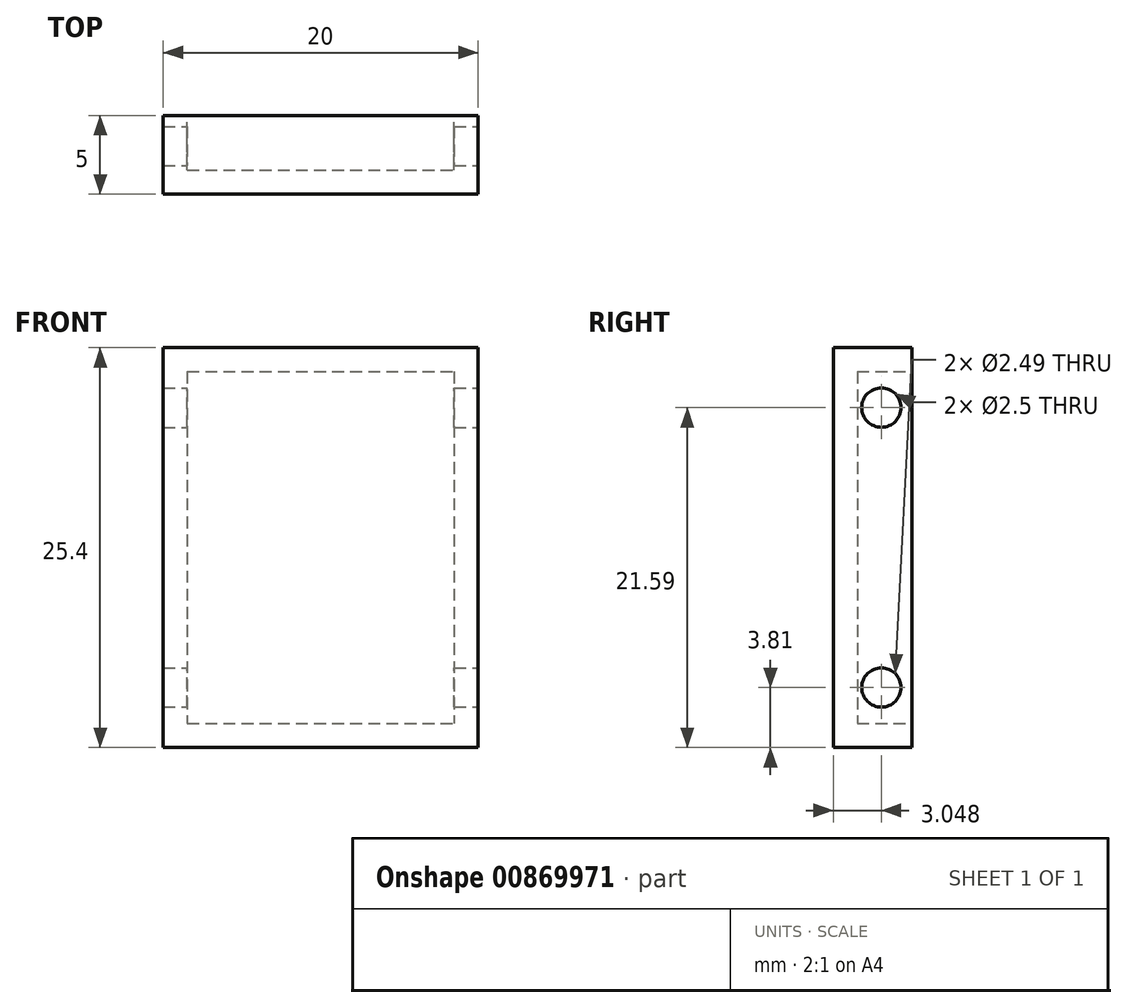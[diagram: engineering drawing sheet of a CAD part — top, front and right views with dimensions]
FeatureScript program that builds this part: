
annotation { "Feature Type Name" : "Feature", "Feature Type Description" : "" }
export const myFeature = defineFeature(function(context is Context, id is Id, definition is map)
    precondition{}
    {
        {
            var Q0;
            Q0=qCreatedBy(makeId("Front.planeOp"),FACE);
            var sketch = newSketch(context, id + "F0", { "sketchPlane" : qUnion([Q0])});
            skLineSegment(sketch, "E0.bottom", {"start": v(-10, 12.7) * mm, "end": v(10, 12.7) * mm});
            skLineSegment(sketch, "E0.top", {"start": v(-10, -12.7) * mm, "end": v(10, -12.7) * mm});
            skLineSegment(sketch, "E0.left", {"start": v(-10, 12.7) * mm, "end": v(-10, -12.7) * mm});
            skLineSegment(sketch, "E0.right", {"start": v(10, 12.7) * mm, "end": v(10, -12.7) * mm});
            skSolve(sketch);
        }
        {
            var Q0;
            Q0 = qSketchRegion(id + "F0", true);
            extrude(context, id + "F1", {"entities" : qUnion([Q0]), "depth" : 5 * mm, "offsetDistance" : 25.4 * mm});
        }
        {
            var Q0;
            Q0=makeQuery(id+"F1.opExtrude","CAP_FACE",FACE,{"disambiguationData":[OSD([sQuery(id+"F0.wireOp",EDGE,"E0.bottom"),sQuery(id+"F0.wireOp",EDGE,"E0.top"),sQuery(id+"F0.wireOp",EDGE,"E0.left"),sQuery(id+"F0.wireOp",EDGE,"E0.right")])],"isStart":true});
            shell(context, id + "F2", {"entities" : qUnion([Q0]), "thickness" : 1.52 * mm});
        }
        {
            var Q0;
            Q0=makeQuery(id+"F1.opExtrude","SWEPT_FACE",FACE,{"disambiguationData":[OSD([sQuery(id+"F0.wireOp",EDGE,"E0.right")])]});
            var sketch = newSketch(context, id + "F3", { "sketchPlane" : qUnion([Q0])});
            skCircle(sketch, "E1", {"center": v(-1.95, 8.89) * mm, "radius": 1.25 * mm});
            skCircle(sketch, "E2", {"center": v(-1.95, -8.9) * mm, "radius": 1.24 * mm});
            skSolve(sketch);
        }
        {
            var Q0;
            Q0=makeQuery(id+"F3.imprint","IMPRINT",FACE,{"disambiguationData":[TD([[makeQuery(id+"F3.imprint","IMPRINT",EDGE,{"derivedFrom":sQuery(id+"F3.wireOp",EDGE,"E1")}),1.0]])]});
            var Q1;
            Q1=makeQuery(id+"F3.imprint","IMPRINT",FACE,{"disambiguationData":[TD([[makeQuery(id+"F3.imprint","IMPRINT",EDGE,{"derivedFrom":sQuery(id+"F3.wireOp",EDGE,"E2")}),1.0]])]});
            extrude(context, id + "F4", {"entities" : qUnion([Q0, Q1]), "operationType" : NewBodyOperationType.REMOVE, "oppositeDirection" : true, "depth" : 25.4 * mm, "offsetDistance" : 25.4 * mm});
        }
    });
